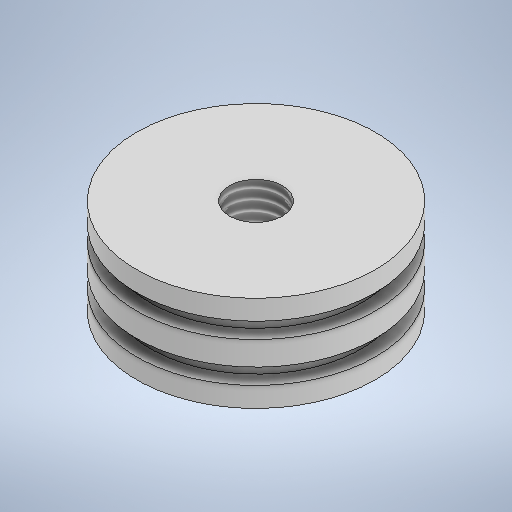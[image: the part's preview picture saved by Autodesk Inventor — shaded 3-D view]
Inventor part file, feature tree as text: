
AUTODESK INVENTOR PART (.ipt)
format: ipt  version: 2025 (Build 290162010, 162A)  size: 267,264 bytes
history: native  units: mm
features: sketch x2, revolve x1, hole x1
ambient origin geometry x8: Origin, YZ Plane, XZ Plane, XY Plane, X Axis, Y Axis, Z Axis, Center Point
bodies: Solid1 (feature_tree)
feature tree (4):
  revolve  "Revolution1"  [1 undecoded]
  hole  "Hole1"  [1 undecoded]
  sketch  "Sketch1"  dims[d0=2.5mm d2=2.5mm]
  sketch  "Sketch2"  dims[d3=2.0mm d4=2.0mm d7=12.0mm d8=26.5mm d9=30.0mm d10=90.0deg d11=6.647mm d12=16.0mm d13=9.0mm d14=5.0mm d15=90.0deg d16=8.0mm d17=20.594885mm]
note: 2 required parameter values undecoded (feature->parameter linkage not recoverable at this tier; creation-order binding heuristic only, values carry confidence <= 0.55)